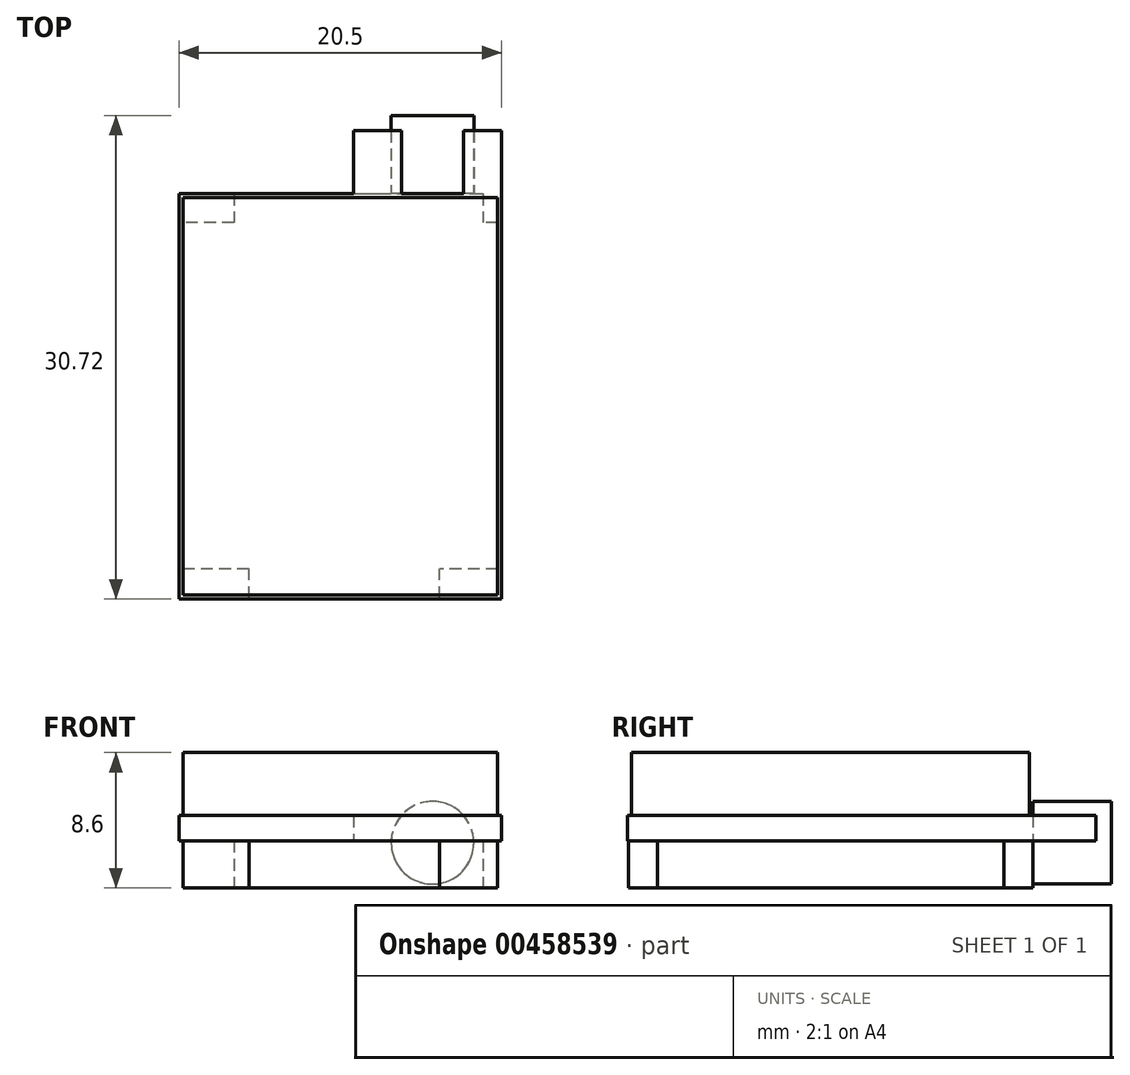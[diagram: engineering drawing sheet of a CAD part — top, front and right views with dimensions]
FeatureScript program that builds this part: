
annotation { "Feature Type Name" : "Feature", "Feature Type Description" : "" }
export const myFeature = defineFeature(function(context is Context, id is Id, definition is map)
    precondition{}
    {
        {
            var Q0;
            Q0=qCreatedBy(makeId("Top.planeOp"),FACE);
            cPlane(context, id + "F0", {"entities" : qUnion([Q0]), "cplaneType" : CPlaneType.OFFSET, "offset" : 3 * mm, "width" : 150 * mm, "height" : 150 * mm});
        }
        {
            var Q0;
            Q0=qCreatedBy(id+"F0.planeOp",FACE);
            var sketch = newSketch(context, id + "F1", { "sketchPlane" : qUnion([Q0])});
            skLineSegment(sketch, "E0.bottom", {"start": v(-10.25, 12.88) * mm, "end": v(10.25, 12.88) * mm});
            skLineSegment(sketch, "E0.top", {"start": v(-10.25, -12.88) * mm, "end": v(10.25, -12.88) * mm});
            skLineSegment(sketch, "E0.left", {"start": v(-10.25, 12.88) * mm, "end": v(-10.25, -12.88) * mm});
            skLineSegment(sketch, "E0.right", {"start": v(10.25, 12.88) * mm, "end": v(10.25, -12.88) * mm});
            skPoint(sketch, "E0.middle", {"position": v(0, 0) * mm});
            skLineSegment(sketch, "E1.bottom", {"start": v(0.85, 16.87) * mm, "end": v(10.25, 16.88) * mm});
            skLineSegment(sketch, "E1.top", {"start": v(0.85, 12.88) * mm, "end": v(10.25, 12.88) * mm});
            skLineSegment(sketch, "E1.left", {"start": v(0.85, 16.87) * mm, "end": v(0.85, 12.87) * mm});
            skLineSegment(sketch, "E1.right", {"start": v(10.25, 16.88) * mm, "end": v(10.25, 12.88) * mm});
            skPoint(sketch, "E1.middle", {"position": v(5.55, 14.87) * mm});
            skSolve(sketch);
        }
        {
            var Q0;
            Q0=qSketchRegion(id+"F1",true);
            extrude(context, id + "F2", {"entities" : qUnion([Q0]), "depth" : 1.6 * mm});
        }
        {
            var Q0;
            Q0=qCreatedBy(makeId("Top.planeOp"),FACE);
            cPlane(context, id + "F3", {"entities" : qUnion([Q0]), "cplaneType" : CPlaneType.OFFSET, "offset" : 0 * mm, "width" : 150 * mm, "height" : 150 * mm});
        }
        {
            var Q0;
            Q0=qCreatedBy(id+"F3.planeOp",FACE);
            var sketch = newSketch(context, id + "F4", { "sketchPlane" : qUnion([Q0])});
            skLineSegment(sketch, "E2.bottom", {"start": v(10, 11.03) * mm, "end": v(-10, 11.03) * mm});
            skLineSegment(sketch, "E2.top", {"start": v(10, -10.97) * mm, "end": v(-10, -10.97) * mm});
            skLineSegment(sketch, "E2.left", {"start": v(10, 11.03) * mm, "end": v(10, -10.97) * mm});
            skLineSegment(sketch, "E2.right", {"start": v(-10, 11.03) * mm, "end": v(-10, -10.97) * mm});
            skPoint(sketch, "E2.middle", {"position": v(0, 0.03) * mm});
            skLineSegment(sketch, "E3.bottom", {"start": v(6.3, -12.83) * mm, "end": v(-5.8, -12.83) * mm});
            skLineSegment(sketch, "E3.top", {"start": v(6.3, -10.98) * mm, "end": v(-5.8, -10.98) * mm});
            skLineSegment(sketch, "E3.left", {"start": v(6.3, -12.83) * mm, "end": v(6.3, -10.98) * mm});
            skLineSegment(sketch, "E3.right", {"start": v(-5.8, -12.83) * mm, "end": v(-5.8, -10.98) * mm});
            skPoint(sketch, "E3.middle", {"position": v(0.25, -11.9) * mm});
            skLineSegment(sketch, "E4.bottom", {"start": v(-6.75, 12.88) * mm, "end": v(9.05, 12.88) * mm});
            skLineSegment(sketch, "E4.top", {"start": v(-6.75, 11.02) * mm, "end": v(9.05, 11.02) * mm});
            skLineSegment(sketch, "E4.left", {"start": v(-6.75, 12.88) * mm, "end": v(-6.75, 11.03) * mm});
            skLineSegment(sketch, "E4.right", {"start": v(9.05, 12.88) * mm, "end": v(9.05, 11.03) * mm});
            skSolve(sketch);
        }
        {
            var Q0;
            Q0=qSketchRegion(id+"F4",true);
            extrude(context, id + "F5", {"entities" : qUnion([Q0]), "depth" : 3 * mm});
        }
        {
            var Q0;
            Q0=makeQuery(id+"F2.opExtrude","SWEPT_FACE",FACE,{"disambiguationData":[OSD([sQuery(id+"F1.wireOp",EDGE,"E0.bottom")])]});
            var sketch = newSketch(context, id + "F6", { "sketchPlane" : qUnion([Q0])});
            skCircle(sketch, "E5", {"center": v(-5.86, 2.88) * mm, "radius": 2.62 * mm});
            skSolve(sketch);
        }
        {
            var Q0;
            Q0=qSketchRegion(id+"F6",true);
            extrude(context, id + "F7", {"entities" : qUnion([Q0]), "operationType" : NewBodyOperationType.ADD, "depth" : 4.96 * mm});
        }
        {
            var Q0;
            Q0=makeQuery(id+"F2.opExtrude","CAP_FACE",FACE,{"disambiguationData":[OSD([sQuery(id+"F1.wireOp",EDGE,"E0.bottom"),sQuery(id+"F1.wireOp",EDGE,"E0.top"),sQuery(id+"F1.wireOp",EDGE,"E0.left"),sQuery(id+"F1.wireOp",EDGE,"E0.right"),sQuery(id+"F1.wireOp",EDGE,"E1.bottom"),sQuery(id+"F1.wireOp",EDGE,"E1.left"),sQuery(id+"F1.wireOp",EDGE,"E1.right")])],"isStart":false});
            var sketch = newSketch(context, id + "F8", { "sketchPlane" : qUnion([Q0])});
            skLineSegment(sketch, "E6.bottom", {"start": v(-10, 12.62) * mm, "end": v(10, 12.62) * mm});
            skLineSegment(sketch, "E6.top", {"start": v(-10, -12.62) * mm, "end": v(10, -12.62) * mm});
            skLineSegment(sketch, "E6.left", {"start": v(-10, 12.62) * mm, "end": v(-10, -12.62) * mm});
            skLineSegment(sketch, "E6.right", {"start": v(10, 12.62) * mm, "end": v(10, -12.62) * mm});
            skSolve(sketch);
        }
        {
            var Q0;
            Q0=qSketchRegion(id+"F8",true);
            extrude(context, id + "F9", {"entities" : qUnion([Q0]), "operationType" : NewBodyOperationType.ADD, "depth" : 4 * mm});
        }
    });
